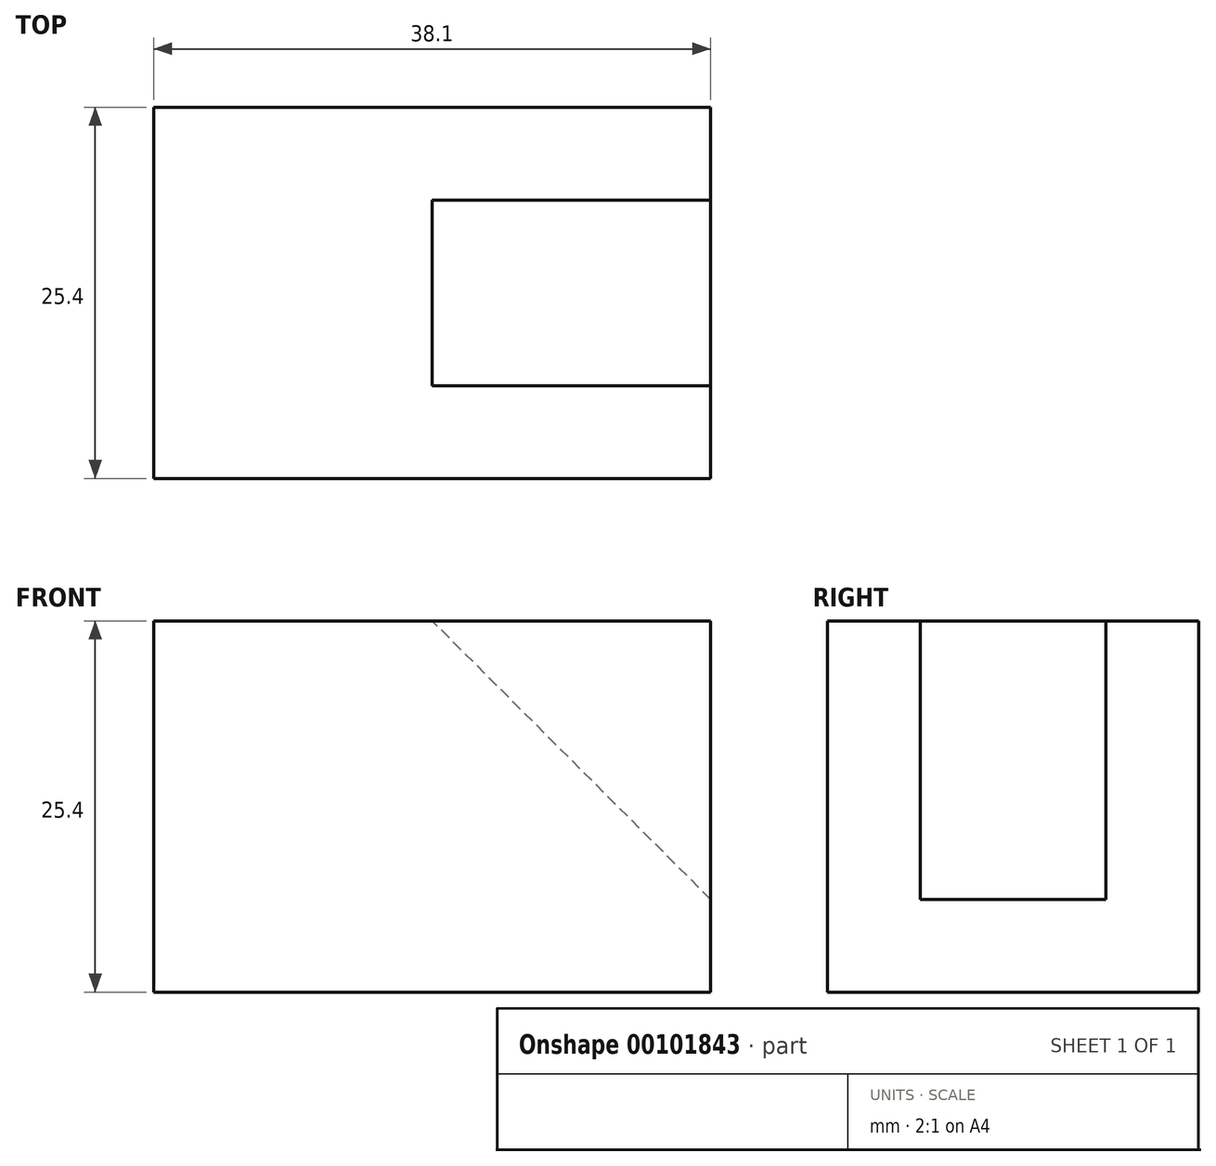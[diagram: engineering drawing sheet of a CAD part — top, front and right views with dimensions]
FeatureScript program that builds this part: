
annotation { "Feature Type Name" : "Feature", "Feature Type Description" : "" }
export const myFeature = defineFeature(function(context is Context, id is Id, definition is map)
    precondition{}
    {
        {
            var Q0;
            Q0=qCreatedBy(makeId("Front.planeOp"),FACE);
            var sketch = newSketch(context, id + "F0", { "sketchPlane" : qUnion([Q0])});
            skLineSegment(sketch, "E0", {"start": v(0, 0) * mm, "end": v(0, 25.4) * mm});
            skLineSegment(sketch, "E1", {"start": v(0, 25.4) * mm, "end": v(38.1, 25.4) * mm});
            skLineSegment(sketch, "E2", {"start": v(38.1, 25.4) * mm, "end": v(38.1, 0) * mm});
            skLineSegment(sketch, "E3", {"start": v(38.1, 0) * mm, "end": v(0, 0) * mm});
            skSolve(sketch);
        }
        {
            var Q0;
            Q0 = qSketchRegion(id + "F0", true);
            extrude(context, id + "F1", {"entities" : qUnion([Q0]), "depth" : 12.7 * mm});
        }
        {
            var Q0;
            Q0=makeQuery(id+"F1.opExtrude","CAP_FACE",FACE,{"disambiguationData":[OSD([sQuery(id+"F0.wireOp",EDGE,"E0"),sQuery(id+"F0.wireOp",EDGE,"E1"),sQuery(id+"F0.wireOp",EDGE,"E2"),sQuery(id+"F0.wireOp",EDGE,"E3")])],"isStart":false});
            var sketch = newSketch(context, id + "F2", { "sketchPlane" : qUnion([Q0])});
            skLineSegment(sketch, "E4", {"start": v(38.1, 6.35) * mm, "end": v(19.05, 25.4) * mm});
            skSolve(sketch);
        }
        {
            var Q0;
            {var subQ0=sQuery(id+"F2.wireOp",EDGE,"E4");Q0=makeQuery(id+"F2.imprint","IMPRINT",FACE,{"disambiguationData":[TD([[makeQuery(id+"F2.imprint","IMPRINT",EDGE,{"derivedFrom":subQ0}),-1.0]])]});}
            extrude(context, id + "F3", {"entities" : qUnion([Q0]), "operationType" : NewBodyOperationType.REMOVE, "endBound" : BoundingType.THROUGH_ALL, "oppositeDirection" : true, "depth" : 12.7 * mm});
        }
        {
            var Q0;
            Q0=makeQuery(id+"F1.opExtrude","CAP_FACE",FACE,{"disambiguationData":[OSD([sQuery(id+"F0.wireOp",EDGE,"E0"),sQuery(id+"F0.wireOp",EDGE,"E1"),sQuery(id+"F0.wireOp",EDGE,"E2"),sQuery(id+"F0.wireOp",EDGE,"E3")])],"isStart":false});
            var sketch = newSketch(context, id + "F4", { "sketchPlane" : qUnion([Q0])});
            skLineSegment(sketch, "E5", {"start": v(0, 25.4) * mm, "end": v(38.1, 25.4) * mm});
            skLineSegment(sketch, "E6", {"start": v(38.1, 25.4) * mm, "end": v(38.1, 0) * mm});
            skLineSegment(sketch, "E7", {"start": v(38.1, 0) * mm, "end": v(0, 0) * mm});
            skLineSegment(sketch, "E8", {"start": v(0, 0) * mm, "end": v(0, 25.4) * mm});
            skSolve(sketch);
        }
        {
            var Q0;
            Q0 = qSketchRegion(id + "F4", true);
            extrude(context, id + "F5", {"entities" : qUnion([Q0]), "operationType" : NewBodyOperationType.ADD, "depth" : 6.35 * mm});
        }
        {
            var Q0;
            Q0=makeQuery(id+"F1.opExtrude","CAP_FACE",FACE,{"disambiguationData":[OSD([sQuery(id+"F0.wireOp",EDGE,"E0"),sQuery(id+"F0.wireOp",EDGE,"E1"),sQuery(id+"F0.wireOp",EDGE,"E2"),sQuery(id+"F0.wireOp",EDGE,"E3")])],"isStart":true});
            var sketch = newSketch(context, id + "F6", { "sketchPlane" : qUnion([Q0])});
            skLineSegment(sketch, "E9", {"start": v(0, 0) * mm, "end": v(0, 25.4) * mm});
            skLineSegment(sketch, "E10", {"start": v(0, 25.4) * mm, "end": v(-38.1, 25.4) * mm});
            skLineSegment(sketch, "E11", {"start": v(-38.1, 25.4) * mm, "end": v(-38.1, 0) * mm});
            skLineSegment(sketch, "E12", {"start": v(-38.1, 0) * mm, "end": v(0, 0) * mm});
            skSolve(sketch);
        }
        {
            var Q0;
            Q0 = qSketchRegion(id + "F6", true);
            extrude(context, id + "F7", {"entities" : qUnion([Q0]), "operationType" : NewBodyOperationType.ADD, "depth" : 6.35 * mm});
        }
    });
